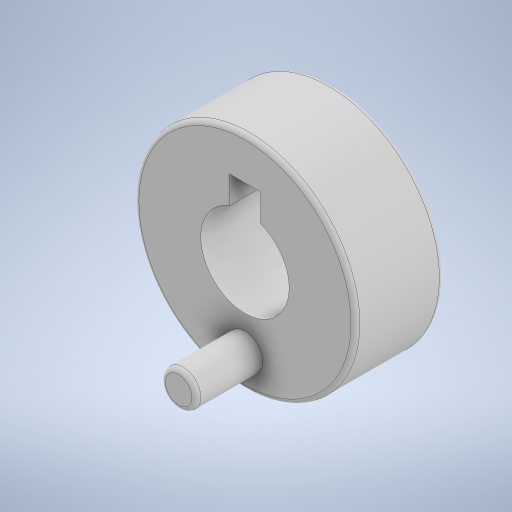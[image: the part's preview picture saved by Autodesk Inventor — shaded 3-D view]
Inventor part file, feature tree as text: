
AUTODESK INVENTOR PART (.ipt)
format: ipt  version: 2024 (Build 280153000, 153)  size: 272,896 bytes
history: native  units: mm
features: extrude x3, sketch x2, other x1, fillet x1
ambient origin geometry x8: Origin, YZ Plane, XZ Plane, XY Plane, X Axis, Y Axis, Z Axis, Center Point
bodies: Body1 (feature_tree)
feature tree (7):
  other  "Sólido1"
  sketch  "Boceto1"  dims[d0=50.0mm d1=20.0mm]
  extrude  "Extrusión1"  Depth=20.0mm
  extrude  "Extrusión2"  Depth=7.0mm
  fillet  "Empalme1"  Radius=35.0mm
  extrude  "Extrusión4"  Depth=20.0mm TaperAngle=0.0deg
  sketch  "Boceto3"  dims[d3=7.5mm d4=8.0mm d5=35.0mm d6=0.0mm d7=20.0mm d8=0.0mm d14=1.0mm d18=15.6mm d19=3.5mm d20=10.0mm d21=7.0mm d22=0.0mm d23=0.0mm d2=0.5mm]
